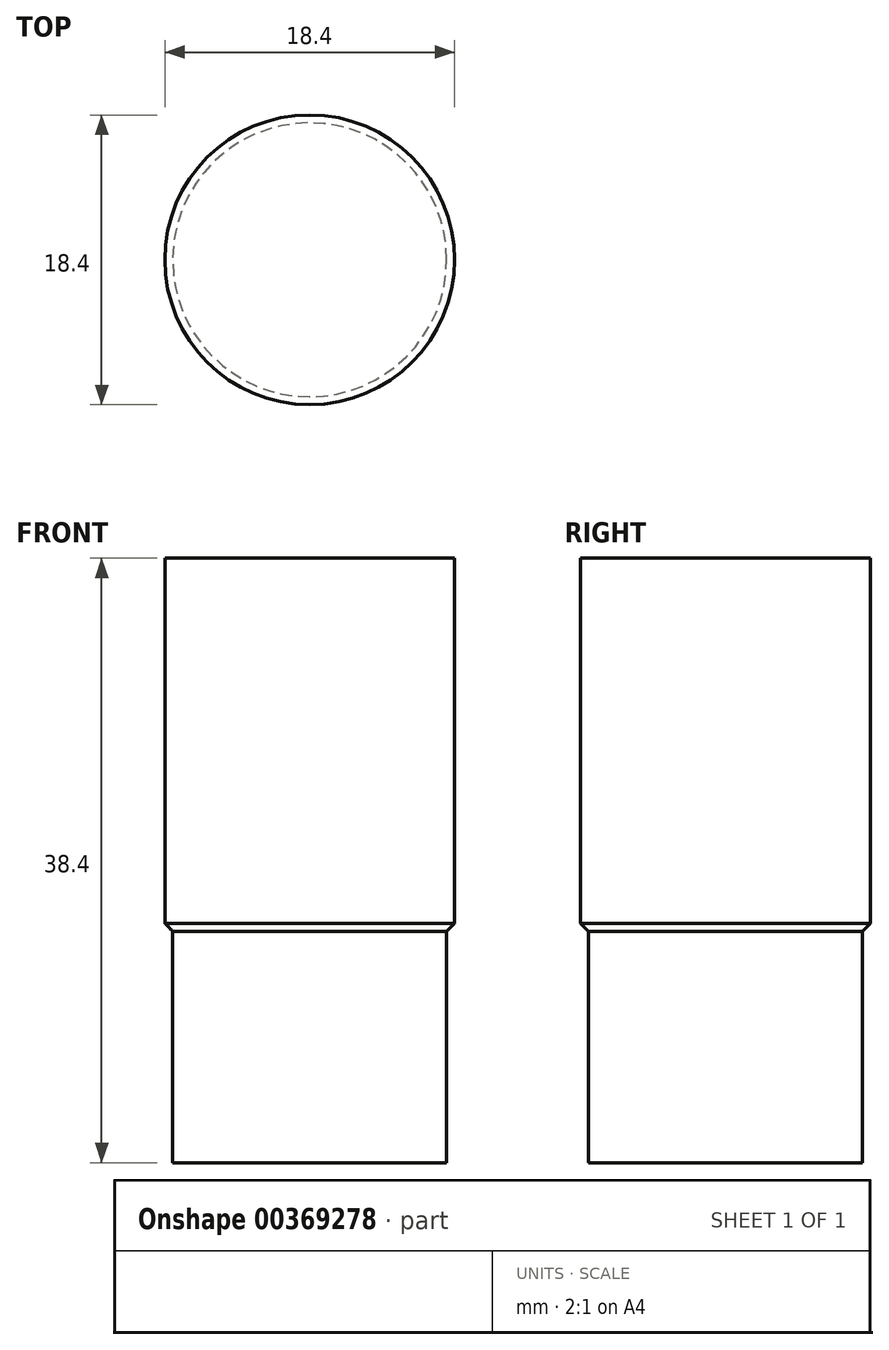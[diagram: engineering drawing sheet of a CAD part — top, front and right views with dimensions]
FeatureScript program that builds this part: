
annotation { "Feature Type Name" : "Feature", "Feature Type Description" : "" }
export const myFeature = defineFeature(function(context is Context, id is Id, definition is map)
    precondition{}
    {
        {
            var Q0;
            Q0=qCreatedBy(makeId("Front.planeOp"),FACE);
            var sketch = newSketch(context, id + "F0", { "sketchPlane" : qUnion([Q0])});
            skLineSegment(sketch, "E0", {"start": v(0, 0) * mm, "end": v(0, 47.07) * mm, "construction": true});
            skLineSegment(sketch, "E1", {"start": v(0, 0) * mm, "end": v(8.7, 0) * mm});
            skLineSegment(sketch, "E2", {"start": v(8.7, 0) * mm, "end": v(8.7, 14.7) * mm});
            skLineSegment(sketch, "E3", {"start": v(8.7, 14.7) * mm, "end": v(9.2, 15.2) * mm});
            skLineSegment(sketch, "E4", {"start": v(9.2, 15.2) * mm, "end": v(9.2, 38.4) * mm});
            skLineSegment(sketch, "E5", {"start": v(9.2, 38.4) * mm, "end": v(0, 38.4) * mm});
            skLineSegment(sketch, "E6", {"start": v(0, 38.4) * mm, "end": v(0, 0) * mm});
            skLineSegment(sketch, "E7", {"start": v(8.7, 14.7) * mm, "end": v(8.7, 20.44) * mm, "construction": true});
            skSolve(sketch);
        }
        {
            var Q0;
            Q0=qSketchRegion(id+"F0",true);
            var Q1;
            Q1=sQuery(id+"F0.wireOp",EDGE,"E0");
            revolve(context, id + "F1", {"entities" : qUnion([Q0]), "axis" : qUnion([Q1]), "revolveType" : RevolveType.FULL});
        }
    });
